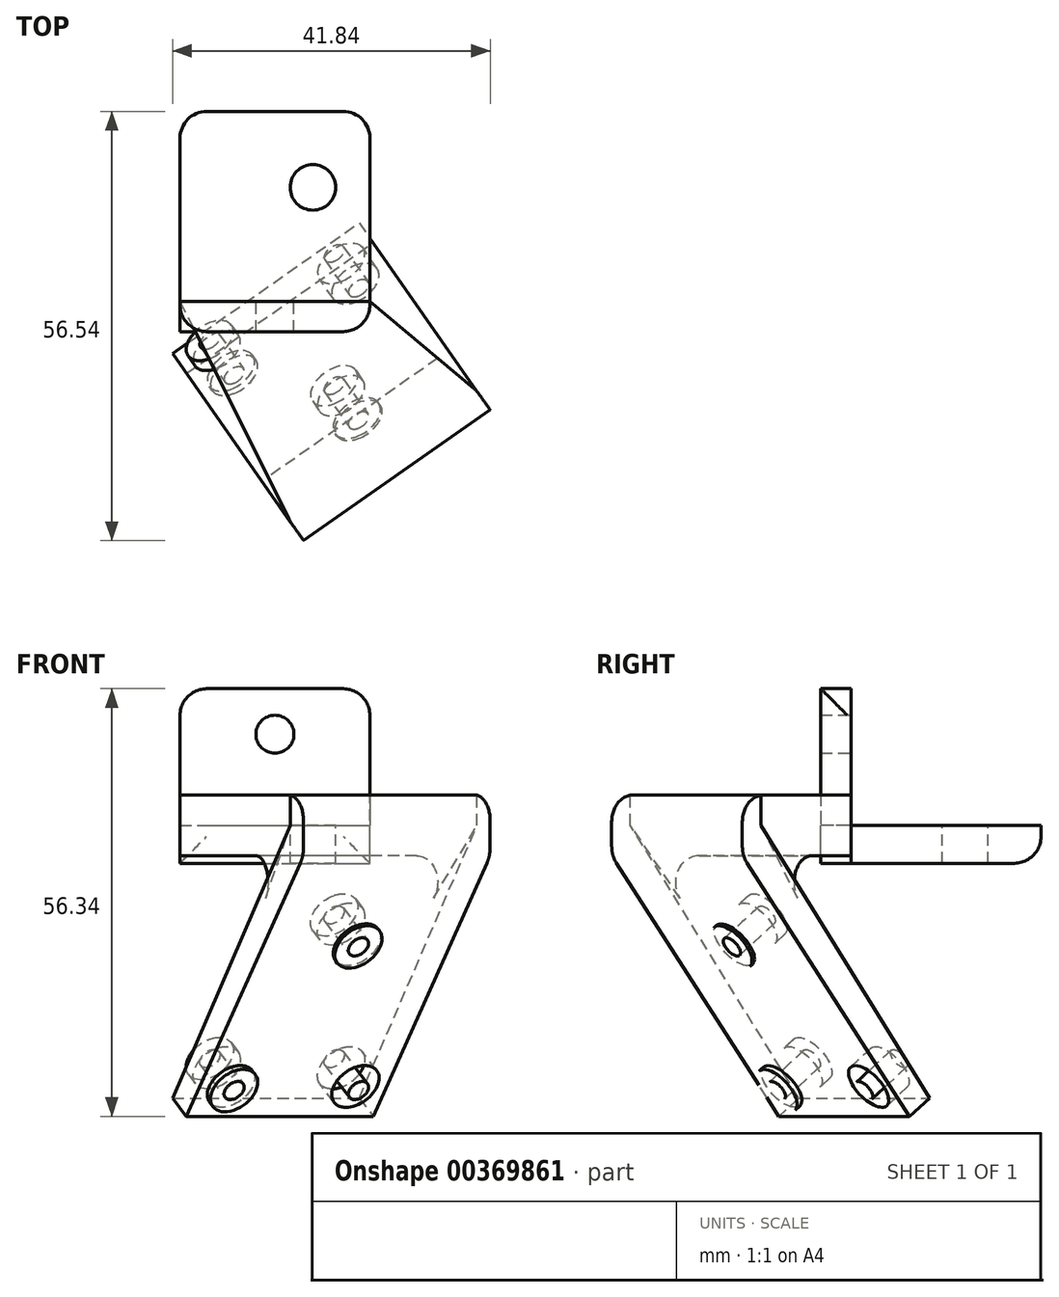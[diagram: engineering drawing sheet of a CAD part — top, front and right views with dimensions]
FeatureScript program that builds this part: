
annotation { "Feature Type Name" : "Feature", "Feature Type Description" : "" }
export const myFeature = defineFeature(function(context is Context, id is Id, definition is map)
    precondition{}
    {
        {
            var Q0;
            Q0=qCreatedBy(makeId("Top.planeOp"),FACE);
            var sketch = newSketch(context, id + "F0", { "sketchPlane" : qUnion([Q0])});
            skLineSegment(sketch, "E0.bottom", {"start": v(-12.5, 0) * mm, "end": v(12.5, 0) * mm});
            skLineSegment(sketch, "E0.top", {"start": v(-12.5, 25) * mm, "end": v(12.5, 25) * mm});
            skLineSegment(sketch, "E0.left", {"start": v(-12.5, 0) * mm, "end": v(-12.5, 25) * mm});
            skLineSegment(sketch, "E0.right", {"start": v(12.5, 0) * mm, "end": v(12.5, 25) * mm});
            skCircle(sketch, "E1", {"center": v(5, 15) * mm, "radius": 3 * mm});
            skLineSegment(sketch, "E2.top", {"start": v(-12.5, -4) * mm, "end": v(12.5, -4) * mm});
            skLineSegment(sketch, "E2.left", {"start": v(-12.5, 0) * mm, "end": v(-12.5, -4) * mm});
            skLineSegment(sketch, "E2.right", {"start": v(12.5, 0) * mm, "end": v(12.5, -4) * mm});
            skSolve(sketch);
        }
        {
            var Q0;
            Q0=makeQuery(id+"F0.imprint","IMPRINT",FACE,{"disambiguationData":[TD([[makeQuery(id+"F0.imprint","IMPRINT",EDGE,{"derivedFrom":sQuery(id+"F0.wireOp",EDGE,"E0.top")}),-1.0]])]});
            extrude(context, id + "F1", {"entities" : qUnion([Q0]), "oppositeDirection" : true, "depth" : 5 * mm});
        }
        {
            var Q0;
            Q0=makeQuery(id+"F0.imprint","IMPRINT",FACE,{"disambiguationData":[TD([[makeQuery(id+"F0.imprint","IMPRINT",EDGE,{"derivedFrom":sQuery(id+"F0.wireOp",EDGE,"E0.bottom")}),-1.0]])]});
            extrude(context, id + "F2", {"entities" : qUnion([Q0]), "depth" : 18 * mm});
        }
        {
            var Q0;
            Q0=makeQuery(id+"F2.opExtrude","CAP_FACE",FACE,{"disambiguationData":[OSD([sQuery(id+"F0.wireOp",EDGE,"E0.bottom"),sQuery(id+"F0.wireOp",EDGE,"E2.top"),sQuery(id+"F0.wireOp",EDGE,"E2.left"),sQuery(id+"F0.wireOp",EDGE,"E2.right")])],"isStart":true});
            extrude(context, id + "F3", {"entities" : qUnion([Q0]), "depth" : 5 * mm});
        }
        {
            var Q0;
            Q0=makeQuery(id+"F2.opExtrude","SWEPT_FACE",FACE,{"disambiguationData":[OSD([sQuery(id+"F0.wireOp",EDGE,"E0.bottom")])]});
            var sketch = newSketch(context, id + "F4", { "sketchPlane" : qUnion([Q0])});
            skCircle(sketch, "E3", {"center": v(0, 12) * mm, "radius": 2.5 * mm});
            skSolve(sketch);
        }
        {
            var Q0;
            Q0=makeQuery(id+"F4.imprint","IMPRINT",FACE,{"disambiguationData":[TD([[makeQuery(id+"F4.imprint","IMPRINT",EDGE,{"derivedFrom":sQuery(id+"F4.wireOp",EDGE,"E3")}),1.0]])]});
            extrude(context, id + "F5", {"entities" : qUnion([Q0]), "operationType" : NewBodyOperationType.REMOVE, "oppositeDirection" : true, "depth" : 4 * mm});
        }
        {
            var Q0;
            Q0=qCreatedBy(makeId("Top.planeOp"),FACE);
            var sketch = newSketch(context, id + "F6", { "sketchPlane" : qUnion([Q0])});
            skLineSegment(sketch, "E4", {"start": v(0, 0) * mm, "end": v(14.34, -20.48) * mm});
            skLineSegment(sketch, "E5", {"start": v(0, 0) * mm, "end": v(-12.5, 0) * mm});
            skLineSegment(sketch, "E6", {"start": v(2.05, -29.08) * mm, "end": v(14.34, -20.48) * mm});
            skLineSegment(sketch, "E7.MirrorCS", {"start": v(26.63, -11.88) * mm, "end": v(14.34, -20.48) * mm});
            skLineSegment(sketch, "E8", {"start": v(0, 0) * mm, "end": v(12.5, 0) * mm});
            skLineSegment(sketch, "E9", {"start": v(2.05, -29.08) * mm, "end": v(-12.5, 0) * mm});
            skLineSegment(sketch, "E10", {"start": v(26.63, -11.88) * mm, "end": v(12.5, 0) * mm});
            skSolve(sketch);
        }
        {
            var Q0;
            Q0=makeQuery(id+"F6.imprint","IMPRINT",FACE,{"disambiguationData":[TD([[makeQuery(id+"F6.imprint","IMPRINT",EDGE,{"derivedFrom":sQuery(id+"F6.wireOp",EDGE,"E4")}),-1.0]])]});
            var Q1;
            Q1=makeQuery(id+"F6.imprint","IMPRINT",FACE,{"disambiguationData":[TD([[makeQuery(id+"F6.imprint","IMPRINT",EDGE,{"derivedFrom":sQuery(id+"F6.wireOp",EDGE,"E4")}),1.0]])]});
            extrude(context, id + "F7", {"entities" : qUnion([Q0, Q1]), "endBound" : BoundingType.SYMMETRIC, "oppositeDirection" : true, "depth" : 8 * mm});
        }
        {
            var Q0;
            Q0=makeQuery(id+"F7.opExtrude","SWEPT_FACE",FACE,{"disambiguationData":[OSD([sQuery(id+"F6.wireOp",EDGE,"E6"),sQuery(id+"F6.wireOp",EDGE,"E7.MirrorCS")])]});
            var sketch = newSketch(context, id + "F8", { "sketchPlane" : qUnion([Q0])});
            skLineSegment(sketch, "E11.bottom", {"start": v(15, -4) * mm, "end": v(-15, -4) * mm});
            skLineSegment(sketch, "E11.top", {"start": v(15, 4) * mm, "end": v(-15, 4) * mm});
            skLineSegment(sketch, "E11.left", {"start": v(15, -4) * mm, "end": v(15, 4) * mm});
            skLineSegment(sketch, "E11.right", {"start": v(-15, -4) * mm, "end": v(-15, 4) * mm});
            skSolve(sketch);
        }
        {
            var Q0;
            Q0=makeQuery(id+"F8.imprint","IMPRINT",FACE,{"disambiguationData":[TD([[makeQuery(id+"F8.imprint","IMPRINT",EDGE,{"derivedFrom":sQuery(id+"F8.wireOp",EDGE,"E11.bottom")}),1.0]])]});
            extrude(context, id + "F9", {"entities" : qUnion([Q0]), "operationType" : NewBodyOperationType.ADD, "depth" : 3 * mm});
        }
        {
            var Q0;
            Q0=makeQuery(id+"F9.opExtrude","SWEPT_FACE",FACE,{"disambiguationData":[OSD([sQuery(id+"F8.wireOp",EDGE,"E11.left")])]});
            var sketch = newSketch(context, id + "F10", { "sketchPlane" : qUnion([Q0])});
            skLineSegment(sketch, "E12", {"start": v(2.1, -35.93) * mm, "end": v(-28, 4) * mm});
            skLineSegment(sketch, "E13", {"start": v(2.1, -35.93) * mm, "end": v(-1.1, -38.34) * mm});
            skLineSegment(sketch, "E14", {"start": v(-1.1, -38.34) * mm, "end": v(-28, -4) * mm});
            skSolve(sketch);
        }
        {
            var Q0;
            Q0=makeQuery(id+"F10.imprint","IMPRINT",FACE,{"disambiguationData":[TD([[makeQuery(id+"F10.imprint","IMPRINT",EDGE,{"derivedFrom":sQuery(id+"F10.wireOp",EDGE,"E12")}),1.0]])]});
            var Q1;
            {var subQ0=sQuery(id+"F10.wireOp",EDGE,"E13");Q1=makeQuery(id+"F10.imprint","IMPRINT",FACE,{"disambiguationData":[TD([[makeQuery(id+"F10.imprint","IMPRINT",EDGE,{"derivedFrom":subQ0}),-1.0]])]});}
            var Q2;
            Q2=makeQuery(id+"F9.opExtrude","SWEPT_FACE",FACE,{"disambiguationData":[OSD([sQuery(id+"F8.wireOp",EDGE,"E11.right")])]});
            extrude(context, id + "F11", {"entities" : qUnion([Q0, Q1]), "operationType" : NewBodyOperationType.ADD, "endBound" : BoundingType.UP_TO_SURFACE, "oppositeDirection" : true, "endBoundEntityFace" : qUnion([Q2]), "depth" : 25 * mm});
        }
        {
            var Q0;
            Q0=makeQuery(id+"F1.opExtrude","CAP_EDGE",EDGE,{"disambiguationData":[OSD([sQuery(id+"F0.wireOp",EDGE,"E0.top")])],"isStart":false});
            var Q1;
            Q1=makeQuery(id+"F2.opExtrude","SWEPT_EDGE",EDGE,{"disambiguationData":[OSD([sQuery(id+"F0.wireOp",EDGE,"E2.top"),sQuery(id+"F0.wireOp",EDGE,"E2.right")])]});
            var Q2;
            Q2=makeQuery(id+"F3.opExtrude","SWEPT_EDGE",EDGE,{"disambiguationData":[OSD([sQuery(id+"F0.wireOp",EDGE,"E2.top"),sQuery(id+"F0.wireOp",EDGE,"E2.right")])]});
            var Q3;
            Q3=makeQuery(id+"F2.opExtrude","CAP_EDGE",EDGE,{"disambiguationData":[OSD([sQuery(id+"F0.wireOp",EDGE,"E2.left")])],"isStart":false});
            var Q4;
            Q4=makeQuery(id+"F1.opExtrude","SWEPT_EDGE",EDGE,{"disambiguationData":[OSD([sQuery(id+"F0.wireOp",EDGE,"E0.top"),sQuery(id+"F0.wireOp",EDGE,"E0.right")])]});
            var Q5;
            Q5=makeQuery(id+"F1.opExtrude","SWEPT_EDGE",EDGE,{"disambiguationData":[OSD([sQuery(id+"F0.wireOp",EDGE,"E0.top"),sQuery(id+"F0.wireOp",EDGE,"E0.left")])]});
            var Q6;
            Q6=makeQuery(id+"F2.opExtrude","CAP_EDGE",EDGE,{"disambiguationData":[OSD([sQuery(id+"F0.wireOp",EDGE,"E2.right")])],"isStart":false});
            var Q7;
            Q7=makeQuery(id+"F2.opExtrude","SWEPT_EDGE",EDGE,{"disambiguationData":[OSD([sQuery(id+"F0.wireOp",EDGE,"E2.top"),sQuery(id+"F0.wireOp",EDGE,"E2.left")])]});
            var Q8;
            Q8=makeQuery(id+"F9.opExtrude","CAP_EDGE",EDGE,{"disambiguationData":[OSD([sQuery(id+"F8.wireOp",EDGE,"E11.top")])],"isStart":false});
            var Q9;
            {var subQ0=sQuery(id+"F8.wireOp",EDGE,"E11.bottom");Q9=makeQuery(id+"F11.boolean.opBoolean","MERGE",EDGE,{"derivedFrom":[makeQuery(id+"F9.opExtrude","CAP_EDGE",EDGE,{"disambiguationData":[OSD([subQ0])],"isStart":false}),makeQuery(id+"F11.opExtrude","SWEPT_EDGE",EDGE,{"disambiguationData":[OSD([subQ0,sQuery(id+"F8.wireOp",EDGE,"E11.left"),sQuery(id+"F10.wireOp",EDGE,"E14")])]})]});}
            var Q10;
            Q10=makeQuery(id+"F11.boolean.opBoolean","INTERSECT",EDGE,{"derivedFrom":[makeQuery(id+"F9.boolean.opBoolean","MERGE",FACE,{"derivedFrom":[makeQuery(id+"F7.opExtrude","CAP_FACE",FACE,{"disambiguationData":[OSD([sQuery(id+"F6.wireOp",EDGE,"E5"),sQuery(id+"F6.wireOp",EDGE,"E6"),sQuery(id+"F6.wireOp",EDGE,"E7.MirrorCS"),sQuery(id+"F6.wireOp",EDGE,"E8"),sQuery(id+"F6.wireOp",EDGE,"E9"),sQuery(id+"F6.wireOp",EDGE,"E10")])],"isStart":false}),makeQuery(id+"F9.opExtrude","SWEPT_FACE",FACE,{"disambiguationData":[OSD([sQuery(id+"F8.wireOp",EDGE,"E11.bottom")])]})]}),makeQuery(id+"F11.opExtrude","SWEPT_FACE",FACE,{"disambiguationData":[OSD([sQuery(id+"F10.wireOp",EDGE,"E12")])]})]});
            fillet(context, id + "F12", {"entities" : qUnion([Q0, Q1, Q2, Q3, Q4, Q5, Q6, Q7, Q8, Q9, Q10]), "radius" : 3.5 * mm, "tangentPropagation" : true, "allowEdgeOverflow" : false});
        }
        {
            var Q0;
            Q0=makeQuery(id+"F11.opExtrude","SWEPT_FACE",FACE,{"disambiguationData":[OSD([sQuery(id+"F10.wireOp",EDGE,"E12")])]});
            var sketch = newSketch(context, id + "F13", { "sketchPlane" : qUnion([Q0])});
            skLineSegment(sketch, "E15", {"start": v(11.63, -27.6) * mm, "end": v(25.45, -21.78) * mm});
            skLineSegment(sketch, "E16.MirrorCS", {"start": v(11.63, -27.6) * mm, "end": v(0.49, -1.16) * mm});
            skCircle(sketch, "E17", {"center": v(0.49, -1.16) * mm, "radius": 1.5 * mm});
            skCircle(sketch, "E18", {"center": v(0.49, -1.16) * mm, "radius": 3.5 * mm});
            skLineSegment(sketch, "E19", {"start": v(9.7, -23) * mm, "end": v(18.9, -19.11) * mm});
            skCircle(sketch, "E20", {"center": v(18.9, -19.11) * mm, "radius": 1.5 * mm});
            skCircle(sketch, "E21", {"center": v(18.9, -19.11) * mm, "radius": 3.5 * mm});
            skCircle(sketch, "E22.MirrorC", {"center": v(0.48, -26.88) * mm, "radius": 1.5 * mm});
            skCircle(sketch, "E23.MirrorC", {"center": v(0.48, -26.88) * mm, "radius": 3.5 * mm});
            skSolve(sketch);
        }
        {
            var Q0;
            Q0=makeQuery(id+"F13.imprint","IMPRINT",FACE,{"disambiguationData":[TD([[makeQuery(id+"F13.imprint","IMPRINT",EDGE,{"derivedFrom":sQuery(id+"F13.wireOp",EDGE,"E17")}),-1.0]])]});
            var Q1;
            Q1=makeQuery(id+"F13.imprint","IMPRINT",FACE,{"disambiguationData":[TD([[makeQuery(id+"F13.imprint","IMPRINT",EDGE,{"derivedFrom":sQuery(id+"F13.wireOp",EDGE,"E22.MirrorC")}),1.0]])]});
            var Q2;
            Q2=makeQuery(id+"F13.imprint","IMPRINT",FACE,{"disambiguationData":[TD([[makeQuery(id+"F13.imprint","IMPRINT",EDGE,{"derivedFrom":sQuery(id+"F13.wireOp",EDGE,"E20")}),-1.0]])]});
            extrude(context, id + "F14", {"entities" : qUnion([Q0, Q1, Q2]), "depth" : 2 * mm});
        }
        {
            var Q0;
            Q0=makeQuery(id+"F13.imprint","IMPRINT",FACE,{"disambiguationData":[TD([[makeQuery(id+"F13.imprint","IMPRINT",EDGE,{"derivedFrom":sQuery(id+"F13.wireOp",EDGE,"E22.MirrorC")}),-1.0]])]});
            var Q1;
            Q1=makeQuery(id+"F13.imprint","IMPRINT",FACE,{"disambiguationData":[TD([[makeQuery(id+"F13.imprint","IMPRINT",EDGE,{"derivedFrom":sQuery(id+"F13.wireOp",EDGE,"E17")}),1.0]])]});
            var Q2;
            Q2=makeQuery(id+"F13.imprint","IMPRINT",FACE,{"disambiguationData":[TD([[makeQuery(id+"F13.imprint","IMPRINT",EDGE,{"derivedFrom":sQuery(id+"F13.wireOp",EDGE,"E20")}),1.0]])]});
            extrude(context, id + "F15", {"entities" : qUnion([Q0, Q1, Q2]), "operationType" : NewBodyOperationType.REMOVE, "endBound" : BoundingType.SYMMETRIC, "oppositeDirection" : true, "depth" : 20 * mm});
        }
        {
            var Q0;
            Q0=makeQuery(id+"F14.opExtrude","CAP_FACE",FACE,{"disambiguationData":[OSD([sQuery(id+"F13.wireOp",EDGE,"E17"),sQuery(id+"F13.wireOp",EDGE,"E18")])],"isStart":false});
            var Q1;
            Q1=makeQuery(id+"F14.opExtrude","CAP_FACE",FACE,{"disambiguationData":[OSD([sQuery(id+"F13.wireOp",EDGE,"E22.MirrorC"),sQuery(id+"F13.wireOp",EDGE,"E23.MirrorC")])],"isStart":false});
            var Q2;
            Q2=makeQuery(id+"F14.opExtrude","CAP_FACE",FACE,{"disambiguationData":[OSD([sQuery(id+"F13.wireOp",EDGE,"E20"),sQuery(id+"F13.wireOp",EDGE,"E21")])],"isStart":false});
            extrude(context, id + "F16", {"entities" : qUnion([Q0, Q1, Q2]), "operationType" : NewBodyOperationType.ADD, "oppositeDirection" : true, "depth" : 7 * mm});
        }
    });
